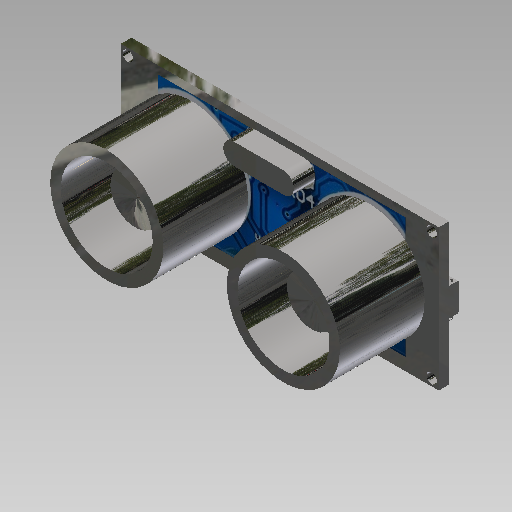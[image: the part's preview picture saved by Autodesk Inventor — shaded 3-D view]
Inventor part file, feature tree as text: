
AUTODESK INVENTOR PART (.ipt)
format: ipt  version: 2020 (Build 240168000, 168)  size: 1,159,168 bytes
history: native  units: mm
features: sketch x18, extrude x12, other x9, pattern_linear x4, projected_geometry x3, chamfer x2, sweep x1, hole x1, revolve x1, mirror x1
ambient origin geometry x8: Origin, YZ Plane, XZ Plane, XY Plane, X Axis, Y Axis, Z Axis, Center Point
bodies: Body1 (feature_tree)
feature tree (52):
  other  "솔리드1"
  extrude  "돌출1"  Depth=45.0mm
  extrude  "돌출2"  Depth=20.0mm
  chamfer  "모따기1"  Distance=1.5mm
  other  "작업 평면1"
  extrude  "돌출3"  Depth=8.5mm
  pattern_linear  "직사각형 패턴1"  Spacing1=4.0mm  [1 undecoded]
  other  "작업 평면2"
  extrude  "돌출4"  Depth=8.5mm
  pattern_linear  "직사각형 패턴2"  Spacing1=0.1mm  [1 undecoded]
  other  "작업 평면3"
  extrude  "돌출5"  Depth=4.0mm
  pattern_linear  "직사각형 패턴3"  Spacing1=9.5mm  [1 undecoded]
  sketch  "스케치6"
  extrude  "돌출6"  Depth=2.0mm
  extrude  "돌출7"  Depth=1.5mm TaperAngle=0.0deg
  chamfer  "모따기2"  Distance=0.2mm Angle=45.0deg
  sweep  "스윕1"
  extrude  "돌출8"  Depth=0.5mm
  hole  "구멍1"  [1 undecoded]
  pattern_linear  "직사각형 패턴4"  Spacing1=0.1mm  [1 undecoded]
  extrude  "돌출9"  Depth=0.05mm
  extrude  "돌출10"  Depth=0.2mm TaperAngle=0.0deg
  extrude  "돌출11"  Depth=7.9mm
  extrude  "돌출12"  [1 undecoded]
  other  "작업 평면4"
  revolve  "회전1"
  mirror  "대칭1"
  other  "전사1"
  other  "전사2"
  sketch  "스케치1"
  sketch  "스케치2"
  sketch  "스케치3"
  sketch  "스케치4"
  projected_geometry  "투영된 루프1"
  projected_geometry  "투영된 루프2"
  sketch  "스케치5"
  sketch  "스케치7"
  projected_geometry  "투영된 루프3"
  sketch  "스케치8"
  sketch  "스케치9"
  sketch  "스케치10"
  sketch  "스케치11"
  sketch  "스케치12"
  sketch  "스케치13"
  sketch  "스케치14"
  sketch  "스케치15"
  sketch  "스케치16"
  sketch  "스케치17"
  other  "이미지1"
  sketch  "스케치18"
  other  "이미지7"
note: 6 required parameter values undecoded (feature->parameter linkage not recoverable at this tier; creation-order binding heuristic only, values carry confidence <= 0.55)
